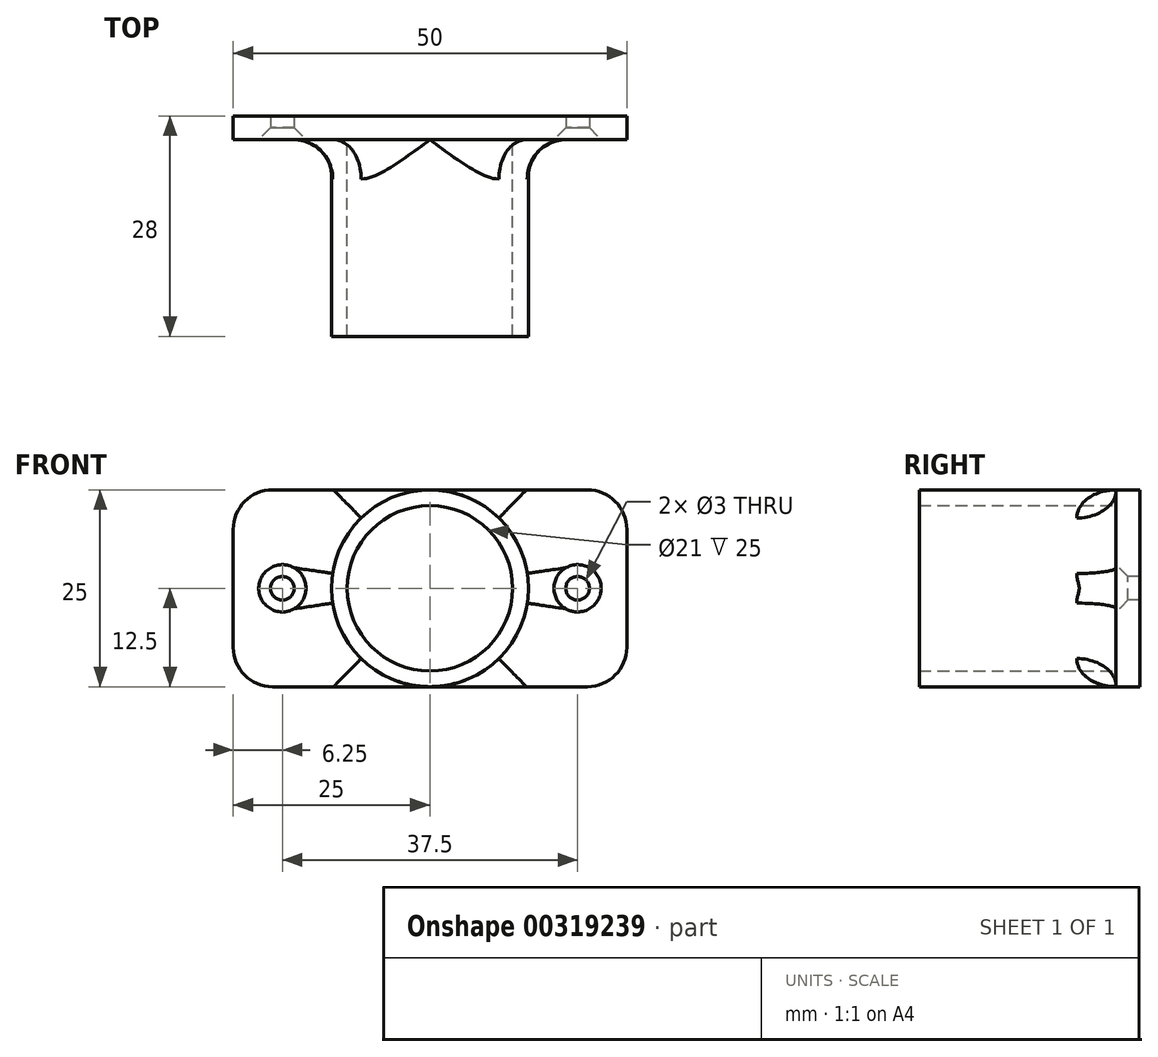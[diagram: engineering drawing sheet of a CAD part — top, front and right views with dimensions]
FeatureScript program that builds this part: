
annotation { "Feature Type Name" : "Feature", "Feature Type Description" : "" }
export const myFeature = defineFeature(function(context is Context, id is Id, definition is map)
    precondition{}
    {
        {
            var Q0;
            Q0=qCreatedBy(makeId("Front.planeOp"),FACE);
            var sketch = newSketch(context, id + "F0", { "sketchPlane" : qUnion([Q0])});
            skCircle(sketch, "E0", {"center": v(0, 0) * mm, "radius": 10.5 * mm});
            skCircle(sketch, "E1", {"center": v(0, 0) * mm, "radius": 12.5 * mm});
            skSolve(sketch);
        }
        {
            var Q0;
            Q0 = qSketchRegion(id + "F0", true);
            extrude(context, id + "F1", {"entities" : qUnion([Q0]), "depth" : 25 * mm});
        }
        {
            var Q0;
            Q0=qCreatedBy(makeId("Front.planeOp"),FACE);
            var sketch = newSketch(context, id + "F2", { "sketchPlane" : qUnion([Q0])});
            skLineSegment(sketch, "E2.bottom", {"start": v(25, 12.5) * mm, "end": v(-25, 12.5) * mm});
            skLineSegment(sketch, "E2.top", {"start": v(25, -12.5) * mm, "end": v(-25, -12.5) * mm});
            skLineSegment(sketch, "E2.left", {"start": v(25, 12.5) * mm, "end": v(25, -12.5) * mm});
            skLineSegment(sketch, "E2.right", {"start": v(-25, 12.5) * mm, "end": v(-25, -12.5) * mm});
            skPoint(sketch, "E2.middle", {"position": v(0, 0) * mm});
            skSolve(sketch);
        }
        {
            var Q0;
            Q0 = qSketchRegion(id + "F2", true);
            extrude(context, id + "F3", {"entities" : qUnion([Q0]), "operationType" : NewBodyOperationType.ADD, "oppositeDirection" : true, "depth" : 3 * mm});
        }
        {
            var Q0;
            {var subQ0=sQuery(id+"F2.wireOp",EDGE,"E2.top");var subQ1=sQuery(id+"F2.wireOp",EDGE,"E2.right");var subQ2=sQuery(id+"F2.wireOp",EDGE,"E2.bottom");var subQ3=makeQuery(id+"F3.opExtrude","CAP_FACE",FACE,{"disambiguationData":[OSD([subQ2,subQ0,sQuery(id+"F2.wireOp",EDGE,"E2.left"),subQ1])],"isStart":true});Q0=makeQuery(id+"F3.boolean.opBoolean","SPLIT",FACE,{"disambiguationData":[TD([makeQuery(id+"F3.opExtrude","SWEPT_FACE",FACE,{"disambiguationData":[OSD([subQ1])]})])],"derivedFrom":subQ3});}
            var sketch = newSketch(context, id + "F4", { "sketchPlane" : qUnion([Q0])});
            skLineSegment(sketch, "E3", {"start": v(-12.5, -12.5) * mm, "end": v(-12.5, 12.5) * mm, "construction": true});
            skLineSegment(sketch, "E4", {"start": v(-12.5, 12.5) * mm, "end": v(-25, -12.5) * mm, "construction": true});
            skPoint(sketch, "E5", {"position": v(-18.75, 0) * mm});
            skSolve(sketch);
        }
        {
            var Q0;
            {var subQ0=sQuery(id+"F2.wireOp",EDGE,"E2.top");var subQ1=sQuery(id+"F2.wireOp",EDGE,"E2.left");var subQ2=sQuery(id+"F2.wireOp",EDGE,"E2.bottom");var subQ3=makeQuery(id+"F3.opExtrude","CAP_FACE",FACE,{"disambiguationData":[OSD([subQ2,subQ0,subQ1,sQuery(id+"F2.wireOp",EDGE,"E2.right")])],"isStart":true});Q0=makeQuery(id+"F3.boolean.opBoolean","SPLIT",FACE,{"disambiguationData":[TD([makeQuery(id+"F3.opExtrude","SWEPT_FACE",FACE,{"disambiguationData":[OSD([subQ1])]})])],"derivedFrom":subQ3});}
            var sketch = newSketch(context, id + "F5", { "sketchPlane" : qUnion([Q0])});
            skLineSegment(sketch, "E6", {"start": v(12.5, -12.5) * mm, "end": v(25, 12.5) * mm, "construction": true});
            skPoint(sketch, "E7", {"position": v(18.75, 0) * mm});
            skSolve(sketch);
        }
        {
            var Q0;
            Q0=sQuery(id+"F4.wireOp",VERTEX,"E5");
            var Q1;
            Q1=sQuery(id+"F5.wireOp",VERTEX,"E7");
            var Q2;
            Q2=makeQuery(id+"F1.opExtrude","SWEPT_BODY",BODY,{"disambiguationData":[OSD([sQuery(id+"F0.wireOp",EDGE,"E0"),sQuery(id+"F0.wireOp",EDGE,"E1")])]});
            hole(context, id + "F6", {"style" : HoleStyle.C_SINK, "endStyle" : HoleEndStyle.THROUGH, "holeDiameter" : 3 * mm, "cSinkDiameter" : 6 * mm, "cSinkAngle" : 90 * degree, "tappedDepth" : 12 * mm, "tapClearance" : 3, "locations" : qUnion([Q0, Q1]), "scope" : qUnion([Q2])});
        }
        {
            var Q0;
            Q0=makeQuery(id+"F3.boolean.opBoolean","SPLIT",EDGE,{"disambiguationData":[OD(1.0)],"derivedFrom":makeQuery(id+"F1.opExtrude","CAP_EDGE",EDGE,{"disambiguationData":[OSD([sQuery(id+"F0.wireOp",EDGE,"E1")])],"isStart":true})});
            fillet(context, id + "F7", {"entities" : qUnion([Q0]), "radius" : 5 * mm, "tangentPropagation" : true, "allowEdgeOverflow" : false});
        }
        {
            var Q0;
            Q0=makeQuery(id+"F3.opExtrude","SWEPT_EDGE",EDGE,{"disambiguationData":[OSD([sQuery(id+"F2.wireOp",EDGE,"E2.top"),sQuery(id+"F2.wireOp",EDGE,"E2.left")])]});
            var Q1;
            Q1=makeQuery(id+"F3.opExtrude","SWEPT_EDGE",EDGE,{"disambiguationData":[OSD([sQuery(id+"F2.wireOp",EDGE,"E2.top"),sQuery(id+"F2.wireOp",EDGE,"E2.right")])]});
            var Q2;
            Q2=makeQuery(id+"F3.opExtrude","SWEPT_EDGE",EDGE,{"disambiguationData":[OSD([sQuery(id+"F2.wireOp",EDGE,"E2.bottom"),sQuery(id+"F2.wireOp",EDGE,"E2.left")])]});
            var Q3;
            Q3=makeQuery(id+"F3.opExtrude","SWEPT_EDGE",EDGE,{"disambiguationData":[OSD([sQuery(id+"F2.wireOp",EDGE,"E2.bottom"),sQuery(id+"F2.wireOp",EDGE,"E2.right")])]});
            fillet(context, id + "F8", {"entities" : qUnion([Q0, Q1, Q2, Q3]), "radius" : 5 * mm, "tangentPropagation" : true, "allowEdgeOverflow" : false});
        }
    });
